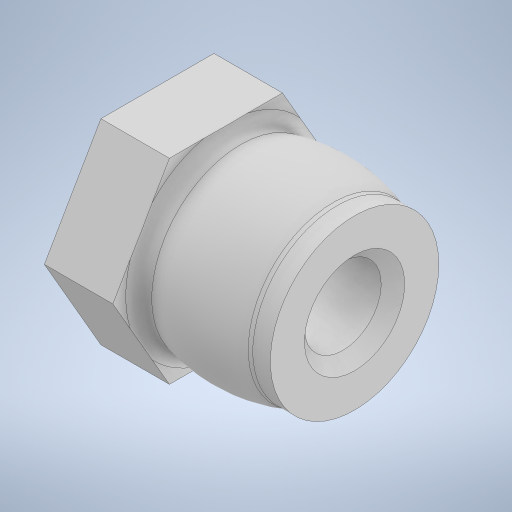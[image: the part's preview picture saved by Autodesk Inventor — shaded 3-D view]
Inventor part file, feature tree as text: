
AUTODESK INVENTOR PART (.ipt)
format: ipt  version: 2024 (Build 280153000, 153)  size: 330,240 bytes
history: native  units: in
note: dims shown in document units (in); Inventor stores cm internally (conversion verified against a paired STEP export)
features: sketch x4, extrude x3, direct_edit x2, other x2, revolve x1, fillet x1, chamfer x1, projected_geometry x1
ambient origin geometry x8: Origin, YZ Plane, XZ Plane, XY Plane, X Axis, Y Axis, Z Axis, Center Point
bodies: Solid1 (feature_tree)
feature tree (15):
  revolve  "Revolution1"  [1 undecoded]
  extrude  "Extrusion1"  Depth=0.2in
  extrude  "Extrusion2"  Depth=0.157in
  fillet  "Fillet1"  Radius=0.0174in
  chamfer  "Chamfer1"  Distance=1.0in
  direct_edit  "Direct Edit1"
  extrude  "Extrusion3"  Depth=0.3937in TaperAngle=0.0deg
  direct_edit  "Direct Edit2"
  sketch  "Sketch1"  dims[d7=0.25in d8=0.098in]
  sketch  "Sketch2"  dims[d9=0.2151in d13=0.2in]
  sketch  "Sketch3"  dims[d14=0.0875in d15=0.157in d17=0.0174in]
  sketch  "Sketch4"  dims[d18=90.0deg d19=1.0in d20=0.0in d21=0.025in d22=0.0in d23=0.015in d24=0.015in d25=0.125in d26=45.0deg d27=3.937in d28=0.3937in d29=0.3937in d30=0.98in d31=1.0in d32=0.0in d33=3.937in d34=0.3937in d35=0.3937in]
  projected_geometry  "Project Cut Edges1"
  other  "Scale1"
  other  "Scale2"
note: 1 required parameter value undecoded (feature->parameter linkage not recoverable at this tier; creation-order binding heuristic only, values carry confidence <= 0.55)
